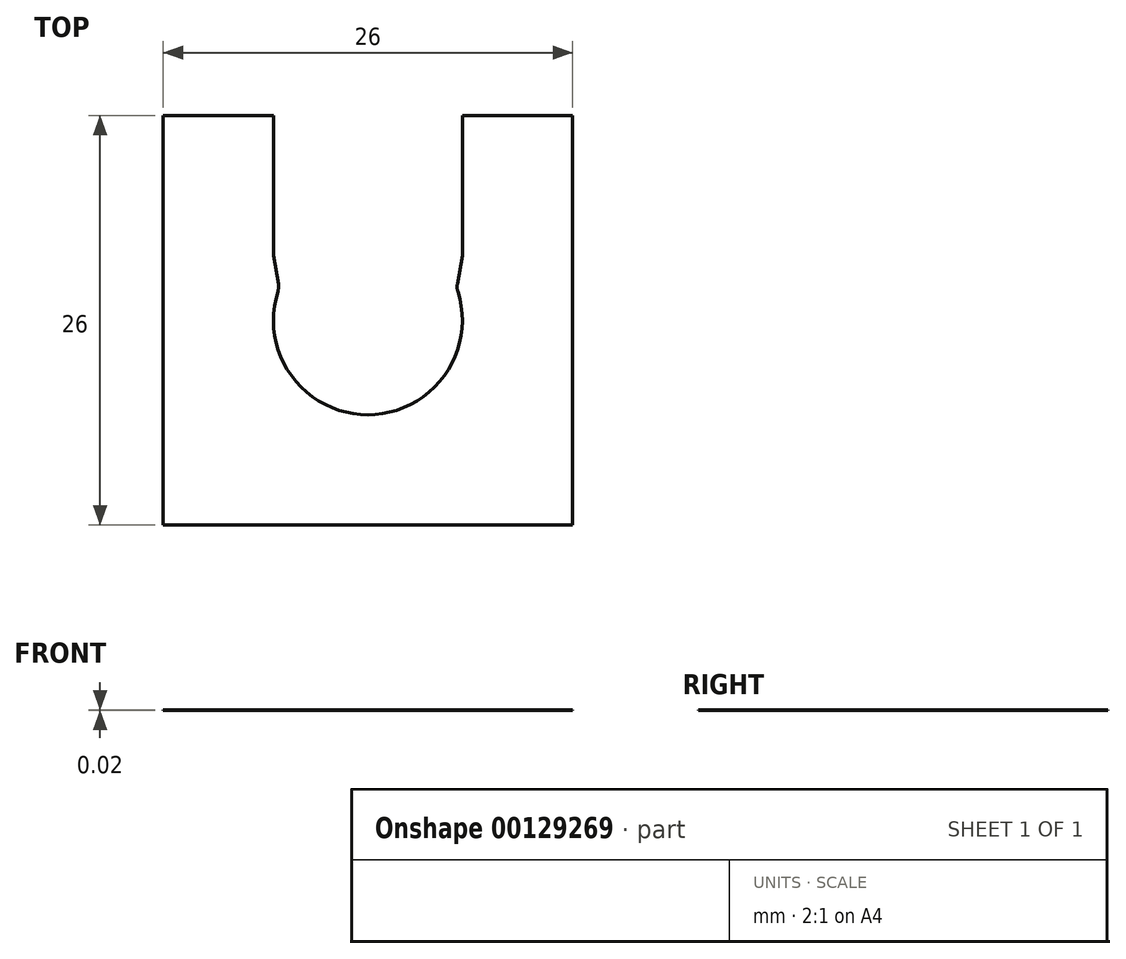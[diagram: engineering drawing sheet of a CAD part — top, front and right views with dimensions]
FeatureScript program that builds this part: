
annotation { "Feature Type Name" : "Feature", "Feature Type Description" : "" }
export const myFeature = defineFeature(function(context is Context, id is Id, definition is map)
    precondition{}
    {
        {
            var Q0;
            Q0=qCreatedBy(makeId("Top.planeOp"),FACE);
            var sketch = newSketch(context, id + "F0", { "sketchPlane" : qUnion([Q0])});
            skLineSegment(sketch, "E0.bottom", {"start": v(-13, 13) * mm, "end": v(-6, 13) * mm});
            skLineSegment(sketch, "E0.top", {"start": v(-13, -13) * mm, "end": v(13, -13) * mm});
            skLineSegment(sketch, "E0.left", {"start": v(-13, 13) * mm, "end": v(-13, -13) * mm});
            skLineSegment(sketch, "E0.right", {"start": v(13, 13) * mm, "end": v(13, -13) * mm});
            skPoint(sketch, "E0.middle", {"position": v(0, 0) * mm});
            skArc(sketch, "E1", {"start": v(-5.72, 1.83) * mm, "mid": v(-5.93, 0.92) * mm, "end": v(-6, 0) * mm});
            skPoint(sketch, "E2", {"position": v(0, -6) * mm});
            skPoint(sketch, "E3", {"position": v(-6, 0) * mm});
            skLineSegment(sketch, "E4", {"start": v(-6, 0) * mm, "end": v(-6, 2.05) * mm, "construction": true});
            skLineSegment(sketch, "E5", {"start": v(-6, 0) * mm, "end": v(0, 0) * mm, "construction": true});
            skLineSegment(sketch, "E6", {"start": v(0, 0) * mm, "end": v(-5.64, 2.05) * mm, "construction": true});
            skLineSegment(sketch, "E7", {"start": v(-5.64, 2.05) * mm, "end": v(-6, 2.05) * mm, "construction": true});
            skLineSegment(sketch, "E8", {"start": v(-6, 2.05) * mm, "end": v(-6, 4.1) * mm, "construction": true});
            skPoint(sketch, "E9.MirrorP", {"position": v(-6, 4.1) * mm});
            skLineSegment(sketch, "E10", {"start": v(-5.68, 2.3) * mm, "end": v(-6, 4.1) * mm});
            skPoint(sketch, "E11.visualSharp", {"position": v(-5.64, 2.05) * mm});
            skArc(sketch, "E11.filletArc", {"start": v(-5.72, 1.83) * mm, "mid": v(-5.67, 2.06) * mm, "end": v(-5.68, 2.3) * mm});
            skLineSegment(sketch, "E12", {"start": v(0, 0) * mm, "end": v(0, -6) * mm, "construction": true});
            skLineSegment(sketch, "E13", {"start": v(-6, 4.1) * mm, "end": v(-6, 13) * mm});
            skLineSegment(sketch, "E14.MirrorCS", {"start": v(6, 4.1) * mm, "end": v(6, 13) * mm});
            skPoint(sketch, "E15.MirrorP", {"position": v(6, 4.1) * mm});
            skLineSegment(sketch, "E16.MirrorCS", {"start": v(5.68, 2.3) * mm, "end": v(6, 4.1) * mm});
            skArc(sketch, "E17.MirrorCS", {"start": v(5.72, 1.83) * mm, "mid": v(5.67, 2.06) * mm, "end": v(5.68, 2.3) * mm});
            skArc(sketch, "E18", {"start": v(-6, 0) * mm, "mid": v(0, -6) * mm, "end": v(6, 0) * mm});
            skArc(sketch, "E19.MirrorCS", {"start": v(5.72, 1.83) * mm, "mid": v(5.93, 0.92) * mm, "end": v(6, 0) * mm});
            skLineSegment(sketch, "E20", {"start": v(-6, 13) * mm, "end": v(6, 13) * mm, "construction": true});
            skLineSegment(sketch, "E21", {"start": v(6, 13) * mm, "end": v(13, 13) * mm});
            skSolve(sketch);
        }
        {
            var Q0;
            Q0=makeQuery(id+"F0.imprint","IMPRINT",FACE,{"disambiguationData":[TD([[makeQuery(id+"F0.imprint","IMPRINT",EDGE,{"derivedFrom":sQuery(id+"F0.wireOp",EDGE,"E0.bottom")}),-1.0]])]});
            extrude(context, id + "F1", {"entities" : qUnion([Q0]), "depth" : 1 / 50.8 * mm});
        }
    });
